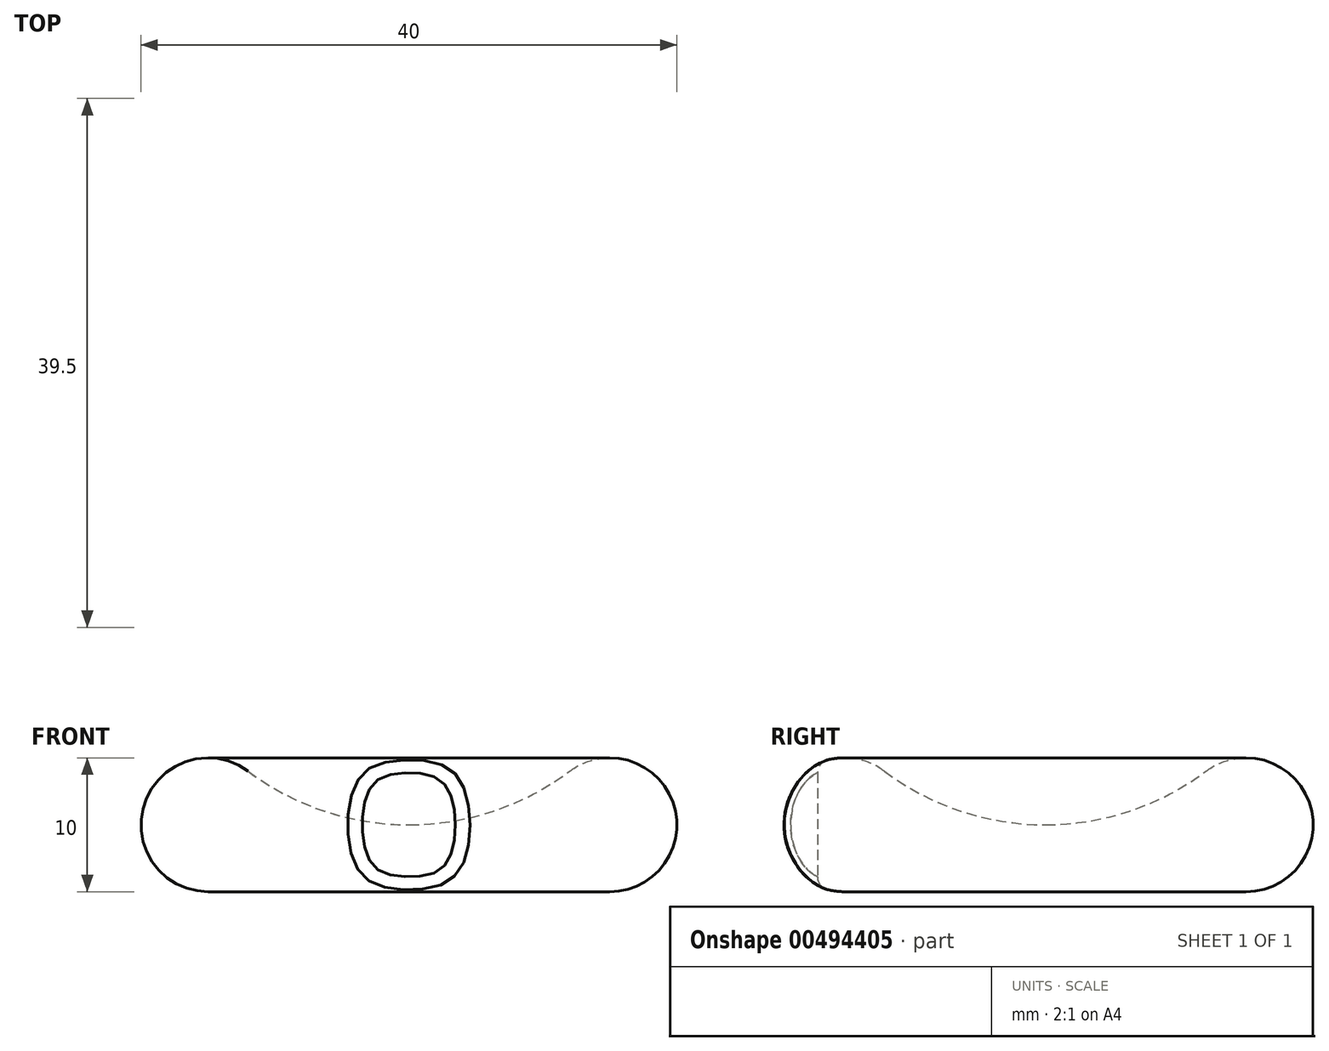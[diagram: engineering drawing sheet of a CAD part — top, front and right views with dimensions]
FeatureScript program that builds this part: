
annotation { "Feature Type Name" : "Feature", "Feature Type Description" : "" }
export const myFeature = defineFeature(function(context is Context, id is Id, definition is map)
    precondition{}
    {
        {
            var Q0;
            Q0=qCreatedBy(makeId("Front.planeOp"),FACE);
            var sketch = newSketch(context, id + "F0", { "sketchPlane" : qUnion([Q0])});
            skArc(sketch, "E0", {"start": v(-12, 9) * mm, "mid": v(-6.32, 6.03) * mm, "end": v(0, 5) * mm});
            skArc(sketch, "E1", {"start": v(-12, 9) * mm, "mid": v(-19.74, 6.58) * mm, "end": v(-15, 0) * mm});
            skLineSegment(sketch, "E2", {"start": v(-15, 0) * mm, "end": v(0, 0) * mm});
            skLineSegment(sketch, "E3", {"start": v(0, 0) * mm, "end": v(0, 5) * mm});
            skSolve(sketch);
        }
        {
            var Q0;
            Q0=makeQuery(id+"F0.imprint","IMPRINT",FACE,{"disambiguationData":[TD([[makeQuery(id+"F0.imprint","IMPRINT",EDGE,{"derivedFrom":sQuery(id+"F0.wireOp",EDGE,"E0")}),-1.0]])]});
            var Q1;
            Q1=sQuery(id+"F0.wireOp",EDGE,"E3");
            revolve(context, id + "F1", {"entities" : qUnion([Q0]), "axis" : qUnion([Q1]), "revolveType" : RevolveType.FULL});
        }
        {
            var Q0;
            Q0=qCreatedBy(makeId("Top.planeOp"),FACE);
            var sketch = newSketch(context, id + "F2", { "sketchPlane" : qUnion([Q0])});
            skCircle(sketch, "E4", {"center": v(0, -21) * mm, "radius": 4 * mm});
            skSolve(sketch);
        }
        {
            var Q0;
            Q0=makeQuery(id+"F2.imprint","IMPRINT",FACE,{"disambiguationData":[TD([[makeQuery(id+"F2.imprint","IMPRINT",EDGE,{"derivedFrom":sQuery(id+"F2.wireOp",EDGE,"E4")}),1.0]])]});
            extrude(context, id + "F3", {"entities" : qUnion([Q0]), "operationType" : NewBodyOperationType.REMOVE, "depth" : 51.82 * mm});
        }
        {
            var Q0;
            Q0=makeQuery(id+"F3.boolean.opBoolean","COPY",FACE,{"derivedFrom":makeQuery(id+"F3.opExtrude","SWEPT_FACE",FACE,{"disambiguationData":[OSD([sQuery(id+"F2.wireOp",EDGE,"E4")])]})});
            fillet(context, id + "F4", {"entities" : qUnion([Q0]), "radius" : 1 * mm, "tangentPropagation" : true, "allowEdgeOverflow" : false});
        }
        {
            var Q0;
            Q0=qCreatedBy(makeId("Top.planeOp"),FACE);
            cPlane(context, id + "F5", {"entities" : qUnion([Q0]), "cplaneType" : CPlaneType.OFFSET, "offset" : 10 * mm, "width" : 150 * mm, "height" : 150 * mm});
        }
    });
